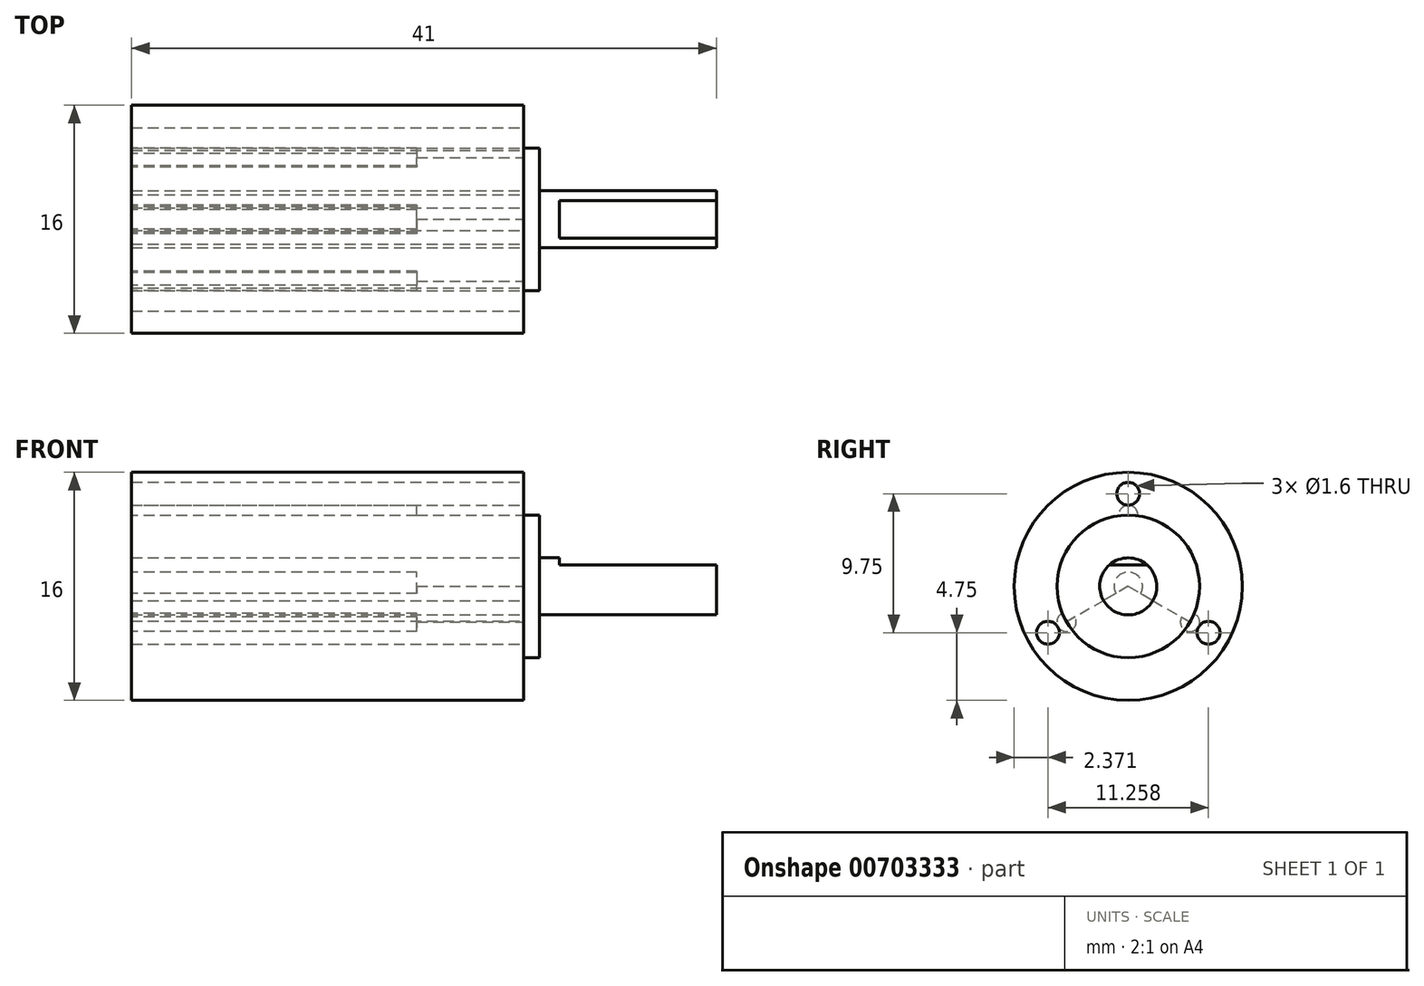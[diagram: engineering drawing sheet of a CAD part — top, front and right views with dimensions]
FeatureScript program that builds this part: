
annotation { "Feature Type Name" : "Feature", "Feature Type Description" : "" }
export const myFeature = defineFeature(function(context is Context, id is Id, definition is map)
    precondition{}
    {
        {
            var Q0;
            Q0=qCreatedBy(makeId("Right.planeOp"),FACE);
            var sketch = newSketch(context, id + "F0", { "sketchPlane" : qUnion([Q0])});
            skCircle(sketch, "E0", {"center": v(0, 0) * mm, "radius": 8 * mm});
            skCircle(sketch, "E1", {"center": v(0, 0) * mm, "radius": 5 * mm});
            skCircle(sketch, "E2", {"center": v(0, 0) * mm, "radius": 2 * mm});
            skLineSegment(sketch, "E3", {"start": v(-1.32, 1.5) * mm, "end": v(1.32, 1.5) * mm});
            skCircle(sketch, "E4", {"center": v(0, 6.5) * mm, "radius": 0.8 * mm});
            skCircle(sketch, "E5", {"center": v(-5.63, -3.25) * mm, "radius": 0.8 * mm});
            skCircle(sketch, "E6", {"center": v(5.63, -3.25) * mm, "radius": 0.8 * mm});
            skLineSegment(sketch, "E7", {"start": v(0, 6.5) * mm, "end": v(0, 0) * mm});
            skLineSegment(sketch, "E8", {"start": v(0, 0) * mm, "end": v(5.63, -3.25) * mm});
            skLineSegment(sketch, "E9", {"start": v(0, 0) * mm, "end": v(-5.63, -3.25) * mm});
            skSolve(sketch);
        }
        {
            var Q0;
            {var subQ0=sQuery(id+"F0.wireOp",EDGE,"E3");Q0=makeQuery(id+"F0.imprint","IMPRINT",FACE,{"disambiguationData":[TD([[makeQuery(id+"F0.imprint","IMPRINT",EDGE,{"derivedFrom":subQ0}),-1.0]])]});}
            var Q1;
            {var subQ0=sQuery(id+"F0.wireOp",EDGE,"E9");var subQ1=sQuery(id+"F0.wireOp",EDGE,"E2");var subQ2=makeQuery(id+"F0.imprint","INTERSECT",VERTEX,{"derivedFrom":[subQ1,subQ0]});Q1=makeQuery(id+"F0.imprint","IMPRINT",FACE,{"disambiguationData":[TD([[makeQuery(id+"F0.imprint","IMPRINT",EDGE,{"disambiguationData":[TD([[subQ2,-1.0]])],"derivedFrom":subQ1}),1.0]])]});}
            extrude(context, id + "F1", {"entities" : qUnion([Q0, Q1]), "depth" : 13.5 * mm, "offsetDistance" : 25 * mm});
        }
        {
            var Q0;
            Q0=makeQuery(id+"F0.imprint","IMPRINT",FACE,{"disambiguationData":[TD([[makeQuery(id+"F0.imprint","IMPRINT",EDGE,{"derivedFrom":sQuery(id+"F0.wireOp",EDGE,"E1")}),1.0]])]});
            var Q1;
            {var subQ1=sQuery(id+"F0.wireOp",EDGE,"E1");var subQ6=sQuery(id+"F0.wireOp",EDGE,"E9");var subQ8=makeQuery(id+"F0.imprint","INTERSECT",VERTEX,{"derivedFrom":[subQ1,subQ6]});Q1=makeQuery(id+"F0.imprint","IMPRINT",FACE,{"disambiguationData":[TD([[makeQuery(id+"F0.imprint","IMPRINT",EDGE,{"disambiguationData":[TD([[subQ8,1.0]])],"derivedFrom":subQ1}),1.0]])]});}
            var Q2;
            {var subQ0=sQuery(id+"F0.wireOp",EDGE,"E7");var subQ1=sQuery(id+"F0.wireOp",EDGE,"E1");var subQ2=makeQuery(id+"F0.imprint","INTERSECT",VERTEX,{"derivedFrom":[subQ1,subQ0]});Q2=makeQuery(id+"F0.imprint","IMPRINT",FACE,{"disambiguationData":[TD([[makeQuery(id+"F0.imprint","IMPRINT",EDGE,{"disambiguationData":[TD([[subQ2,1.0]])],"derivedFrom":subQ1}),1.0]])]});}
            extrude(context, id + "F2", {"entities" : qUnion([Q0, Q1, Q2]), "operationType" : NewBodyOperationType.ADD, "depth" : 1.1 * mm, "offsetDistance" : 25 * mm});
        }
        {
            var Q0;
            Q0=makeQuery(id+"F0.imprint","IMPRINT",FACE,{"disambiguationData":[TD([[makeQuery(id+"F0.imprint","IMPRINT",EDGE,{"derivedFrom":sQuery(id+"F0.wireOp",EDGE,"E0")}),1.0]])]});
            var Q1;
            Q1=makeQuery(id+"F0.imprint","IMPRINT",FACE,{"disambiguationData":[TD([[makeQuery(id+"F0.imprint","IMPRINT",EDGE,{"derivedFrom":sQuery(id+"F0.wireOp",EDGE,"E1")}),1.0]])]});
            var Q2;
            {var subQ0=sQuery(id+"F0.wireOp",EDGE,"E3");Q2=makeQuery(id+"F0.imprint","IMPRINT",FACE,{"disambiguationData":[TD([[makeQuery(id+"F0.imprint","IMPRINT",EDGE,{"derivedFrom":subQ0}),-1.0]])]});}
            var Q3;
            {var subQ0=sQuery(id+"F0.wireOp",EDGE,"E3");Q3=makeQuery(id+"F0.imprint","IMPRINT",FACE,{"disambiguationData":[TD([[makeQuery(id+"F0.imprint","IMPRINT",EDGE,{"derivedFrom":subQ0}),1.0]])]});}
            extrude(context, id + "F3", {"entities" : qUnion([Q0, Q1, Q2, Q3]), "oppositeDirection" : true, "depth" : 27.5 * mm, "offsetDistance" : 25 * mm});
        }
        {
            var Q0;
            Q0=makeQuery(id+"F3.opExtrude","CAP_FACE",FACE,{"disambiguationData":[OSD([sQuery(id+"F0.wireOp",EDGE,"E0"),sQuery(id+"F0.wireOp",EDGE,"E4"),sQuery(id+"F0.wireOp",EDGE,"E5"),sQuery(id+"F0.wireOp",EDGE,"E6")])],"isStart":false});
            var sketch = newSketch(context, id + "F4", { "sketchPlane" : qUnion([Q0])});
            skCircle(sketch, "E10", {"center": v(0, 0) * mm, "radius": 1 * mm});
            skCircle(sketch, "E11", {"center": v(0, 5) * mm, "radius": 0.68 * mm});
            skCircle(sketch, "E12", {"center": v(4.33, -2.5) * mm, "radius": 0.68 * mm});
            skCircle(sketch, "E13", {"center": v(-4.33, -2.5) * mm, "radius": 0.68 * mm});
            skSolve(sketch);
        }
        {
            var Q0;
            Q0=makeQuery(id+"F4.imprint","IMPRINT",FACE,{"disambiguationData":[TD([[makeQuery(id+"F4.imprint","IMPRINT",EDGE,{"derivedFrom":sQuery(id+"F4.wireOp",EDGE,"E10")}),1.0]])]});
            extrude(context, id + "F5", {"entities" : qUnion([Q0]), "operationType" : NewBodyOperationType.REMOVE, "oppositeDirection" : true, "depth" : 20 * mm, "offsetDistance" : 25 * mm});
        }
        {
            var Q0;
            Q0=makeQuery(id+"F4.imprint","IMPRINT",FACE,{"disambiguationData":[TD([[makeQuery(id+"F4.imprint","IMPRINT",EDGE,{"derivedFrom":sQuery(id+"F4.wireOp",EDGE,"E13")}),1.0]])]});
            var Q1;
            Q1=makeQuery(id+"F4.imprint","IMPRINT",FACE,{"disambiguationData":[TD([[makeQuery(id+"F4.imprint","IMPRINT",EDGE,{"derivedFrom":sQuery(id+"F4.wireOp",EDGE,"E11")}),1.0]])]});
            var Q2;
            Q2=makeQuery(id+"F4.imprint","IMPRINT",FACE,{"disambiguationData":[TD([[makeQuery(id+"F4.imprint","IMPRINT",EDGE,{"derivedFrom":sQuery(id+"F4.wireOp",EDGE,"E12")}),1.0]])]});
            extrude(context, id + "F6", {"entities" : qUnion([Q0, Q1, Q2]), "operationType" : NewBodyOperationType.REMOVE, "oppositeDirection" : true, "depth" : 20 * mm, "offsetDistance" : 25 * mm});
        }
        {
            var Q0;
            {var subQ0=sQuery(id+"F0.wireOp",EDGE,"E3");Q0=makeQuery(id+"F0.imprint","IMPRINT",FACE,{"disambiguationData":[TD([[makeQuery(id+"F0.imprint","IMPRINT",EDGE,{"derivedFrom":subQ0}),1.0]])]});}
            extrude(context, id + "F7", {"entities" : qUnion([Q0]), "operationType" : NewBodyOperationType.ADD, "depth" : 2.5 * mm, "offsetDistance" : 25 * mm});
        }
    });
